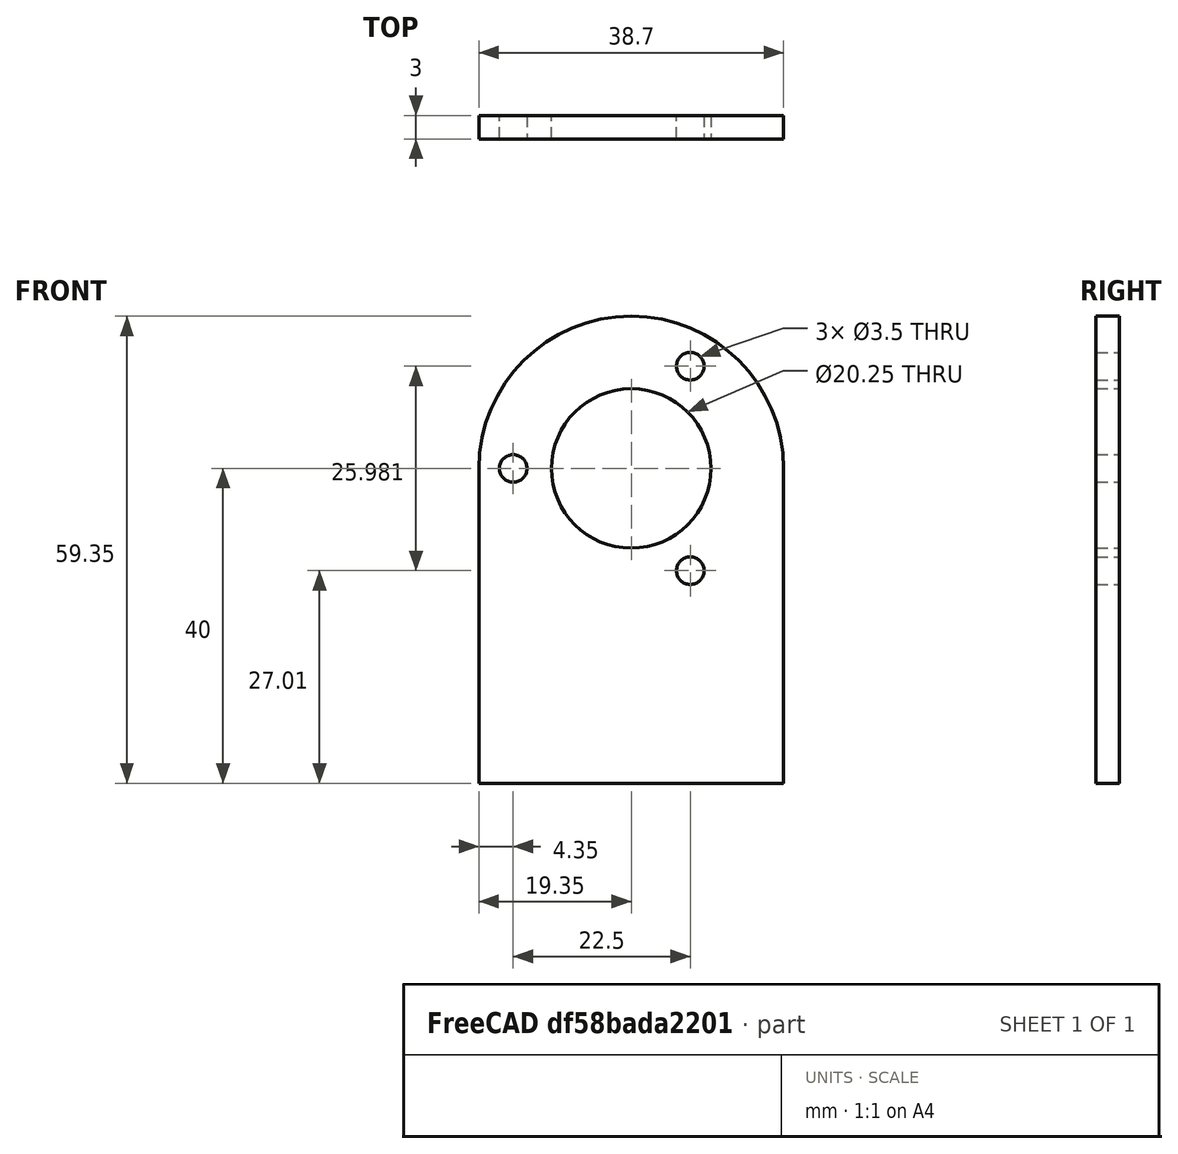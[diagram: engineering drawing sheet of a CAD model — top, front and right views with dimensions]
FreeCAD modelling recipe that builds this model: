
FCSTD DOCUMENT  (FreeCAD 1.0R39319 (Git))
Label: z encoder mount
License: All rights reserved
LicenseURL: https://en.wikipedia.org/wiki/All_rights_reserved
objects: Sketcher::SketchObject×1, PartDesign::Pad×1, PartDesign::Body×1
note: 6 computed .brp shape members not serialized (recipe doc carries the construction recipe); baked Part::Feature solids carry a one-line shape summary decoded from their .brp

FEATURE [Sketcher::SketchObject] Sketch
  ArcFitTolerance = 1e-06
  AttachmentSupport = -> [XZ_Plane]
  FullyConstrained = true
  MakeInternals = false
  MapMode = 5
  Placement = pos=(0,0,0) rot=(1,0,0;1.5708rad)
  sketch-geometry (12):
    g0: Circle CenterX=0 CenterY=0 CenterZ=0 NormalX=0 NormalY=0 NormalZ=1 AngleXU=0 Radius=10.125
    g1: Circle CenterX=7.5 CenterY=12.9904 CenterZ=0 NormalX=0 NormalY=0 NormalZ=1 AngleXU=0 Radius=1.75
    g2: Circle [constr] CenterX=0 CenterY=0 CenterZ=0 NormalX=0 NormalY=0 NormalZ=1 AngleXU=0 Radius=15
    g3: Circle CenterX=-15 CenterY=5.17241e-06 CenterZ=0 NormalX=0 NormalY=0 NormalZ=1 AngleXU=0 Radius=1.75
    g4: Circle CenterX=7.49999 CenterY=-12.9904 CenterZ=0 NormalX=0 NormalY=0 NormalZ=1 AngleXU=0 Radius=1.75
    g5: ArcOfCircle CenterX=0 CenterY=0 CenterZ=0 NormalX=0 NormalY=0 NormalZ=1 AngleXU=0 Radius=19.35 StartAngle=6.28319 EndAngle=9.42478
    g6: LineSegment StartX=-19.35 StartY=-3.35152e-06 StartZ=0 EndX=-19.35 EndY=-40 EndZ=0
    g7: LineSegment StartX=-19.35 StartY=-40 StartZ=0 EndX=19.35 EndY=-40 EndZ=0
    g8: LineSegment StartX=19.35 StartY=-40 StartZ=0 EndX=19.35 EndY=-3.35152e-06 EndZ=0
    g9: LineSegment [constr] StartX=0 StartY=0 StartZ=0 EndX=12.355 EndY=21.3995 EndZ=0
    g10: LineSegment [constr] StartX=0 StartY=0 StartZ=0 EndX=14.115 EndY=-24.4479 EndZ=0
    g11: LineSegment [constr] StartX=0 StartY=0 StartZ=0 EndX=-26.1 EndY=9e-06 EndZ=0
  constraints (28):
    c: Coincident(g0,g-1)
    c: Diameter(g0) = 20.25
    c: Diameter(g1) = 3.5
    c: Diameter(g2) = 30
    c: Coincident(g2,g0)
    c: PointOnObject(g1,g2)
    c: Diameter(g3) = 3.5
    c: Diameter(g4) = 3.5
    c: PointOnObject(g3,g2)
    c: PointOnObject(g4,g2)
    c: Angle(g5) = 3.14159
    c: Coincident(g5,g0)
    c: Distance(g6) = 40
    c: Vertical(g6)
    c: Coincident(g6,g5)
    c: Distance(g7) = 38.7
    c: Horizontal(g7)
    c: Coincident(g7,g6)
    c: Coincident(g8,g7)
    c: Coincident(g8,g5)
    c: Vertical(g8)
    c: DistanceY(g8,g8) = 40
    c: Block(g9)
    c: Block(g11)
    c: Block(g10)
    c: Perpendicular(g1,g9)
    c: Perpendicular(g4,g10)
    c: Perpendicular(g3,g11)
FEATURE [PartDesign::Pad] Pad
  Direction = (0,-1,2e-16)
  Length = 3
  Length2 = 10
  Placement = pos=(0,0,0) rot=(1,0,0;1.5708rad)
  Profile = -> Sketch
  ReferenceAxis = -> Sketch [N_Axis]
  Refine = true
  Suppressed = false
  Type = 0
FEATURE [PartDesign::Body] Body
  AllowCompound = false
  Group = -> [Sketch,Pad]
  Origin = -> Origin
  Tip = -> Pad
